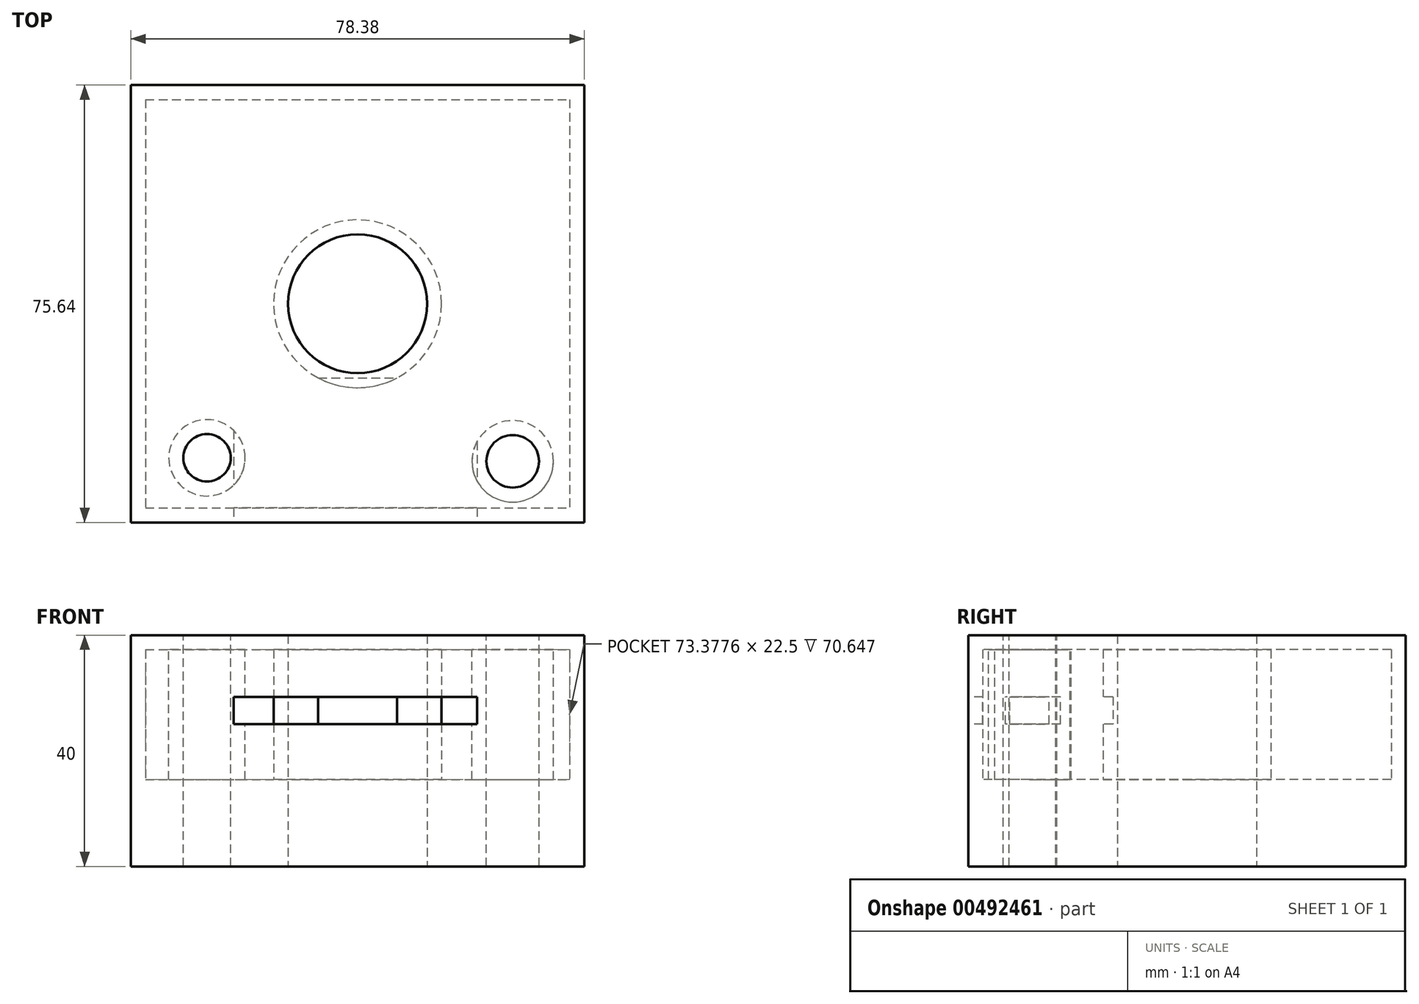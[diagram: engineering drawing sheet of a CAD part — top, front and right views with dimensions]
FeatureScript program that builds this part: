
annotation { "Feature Type Name" : "Feature", "Feature Type Description" : "" }
export const myFeature = defineFeature(function(context is Context, id is Id, definition is map)
    precondition{}
    {
        {
            var Q0;
            Q0=qCreatedBy(makeId("Top.planeOp"),FACE);
            var sketch = newSketch(context, id + "F0", { "sketchPlane" : qUnion([Q0])});
            skLineSegment(sketch, "E0.bottom", {"start": v(-39.19, 37.82) * mm, "end": v(39.19, 37.82) * mm});
            skLineSegment(sketch, "E0.top", {"start": v(-39.19, -37.82) * mm, "end": v(39.19, -37.82) * mm});
            skLineSegment(sketch, "E0.left", {"start": v(-39.19, 37.82) * mm, "end": v(-39.19, -37.82) * mm});
            skLineSegment(sketch, "E0.right", {"start": v(39.19, 37.82) * mm, "end": v(39.19, -37.82) * mm});
            skPoint(sketch, "E0.middle", {"position": v(0, 0) * mm});
            skSolve(sketch);
        }
        {
            var Q0;
            Q0 = qSketchRegion(id + "F0", true);
            extrude(context, id + "F1", {"entities" : qUnion([Q0]), "depth" : 25 * mm});
        }
        {
            var Q0;
            Q0=makeQuery(id+"F1.opExtrude","CAP_FACE",FACE,{"disambiguationData":[OSD([sQuery(id+"F0.wireOp",EDGE,"E0.bottom"),sQuery(id+"F0.wireOp",EDGE,"E0.top"),sQuery(id+"F0.wireOp",EDGE,"E0.left"),sQuery(id+"F0.wireOp",EDGE,"E0.right")])],"isStart":true});
            var sketch = newSketch(context, id + "F2", { "sketchPlane" : qUnion([Q0])});
            skCircle(sketch, "E1", {"center": v(0, 0) * mm, "radius": 12.02 * mm});
            skSolve(sketch);
        }
        {
            var Q0;
            Q0 = qSketchRegion(id + "F2", true);
            extrude(context, id + "F3", {"entities" : qUnion([Q0]), "operationType" : NewBodyOperationType.REMOVE, "oppositeDirection" : true, "depth" : 49.9 * mm});
        }
        {
            var Q0;
            Q0=makeQuery(id+"F1.opExtrude","CAP_FACE",FACE,{"disambiguationData":[OSD([sQuery(id+"F0.wireOp",EDGE,"E0.bottom"),sQuery(id+"F0.wireOp",EDGE,"E0.top"),sQuery(id+"F0.wireOp",EDGE,"E0.left"),sQuery(id+"F0.wireOp",EDGE,"E0.right")])],"isStart":true});
            shell(context, id + "F4", {"entities" : qUnion([Q0]), "thickness" : 2.5 * mm});
        }
        {
            var Q0;
            {var subQ0=sQuery(id+"F0.wireOp",EDGE,"E0.right");var subQ1=sQuery(id+"F0.wireOp",EDGE,"E0.left");var subQ2=sQuery(id+"F0.wireOp",EDGE,"E0.top");var subQ3=sQuery(id+"F0.wireOp",EDGE,"E0.bottom");Q0=makeQuery(id+"F4.opShell","OFFSET_FACE",FACE,{"disambiguationData":[OSD([subQ3,subQ2,subQ1,subQ0]),TDD([makeQuery(id+"F1.opExtrude","CAP_FACE",FACE,{"disambiguationData":[OSD([subQ3,subQ2,subQ1,subQ0])],"isStart":false})])]});}
            var sketch = newSketch(context, id + "F5", { "sketchPlane" : qUnion([Q0])});
            skCircle(sketch, "E2", {"center": v(-26.05, 26.65) * mm, "radius": 6.6 * mm});
            skSolve(sketch);
        }
        {
            var Q0;
            Q0 = qSketchRegion(id + "F5", true);
            extrude(context, id + "F6", {"entities" : qUnion([Q0]), "operationType" : NewBodyOperationType.ADD, "depth" : 25 * mm});
        }
        {
            var Q0;
            Q0=makeQuery(id+"F6.opExtrude","CAP_FACE",FACE,{"disambiguationData":[OSD([sQuery(id+"F5.wireOp",EDGE,"E2")])],"isStart":false});
            shell(context, id + "F7", {"entities" : qUnion([Q0]), "thickness" : 2.5 * mm});
        }
        {
            var Q0;
            Q0=makeQuery(id+"F7.opShell","OFFSET_FACE",FACE,{"disambiguationData":[OSD([sQuery(id+"F0.wireOp",EDGE,"E0.bottom"),sQuery(id+"F0.wireOp",EDGE,"E0.top"),sQuery(id+"F0.wireOp",EDGE,"E0.left"),sQuery(id+"F0.wireOp",EDGE,"E0.right")])]});
            extrude(context, id + "F8", {"entities" : qUnion([Q0]), "operationType" : NewBodyOperationType.REMOVE, "oppositeDirection" : true, "depth" : 25 * mm});
        }
        {
            var Q0;
            {var subQ0=sQuery(id+"F0.wireOp",EDGE,"E0.right");var subQ1=sQuery(id+"F0.wireOp",EDGE,"E0.left");var subQ2=sQuery(id+"F0.wireOp",EDGE,"E0.top");var subQ3=sQuery(id+"F0.wireOp",EDGE,"E0.bottom");Q0=makeQuery(id+"F4.opShell","OFFSET_FACE",FACE,{"disambiguationData":[OSD([subQ3,subQ2,subQ1,subQ0]),TDD([makeQuery(id+"F1.opExtrude","CAP_FACE",FACE,{"disambiguationData":[OSD([subQ3,subQ2,subQ1,subQ0])],"isStart":false})])]});}
            var sketch = newSketch(context, id + "F9", { "sketchPlane" : qUnion([Q0])});
            skCircle(sketch, "E3", {"center": v(26.83, 27.25) * mm, "radius": 7.05 * mm});
            skSolve(sketch);
        }
        {
            var Q0;
            Q0 = qSketchRegion(id + "F9", true);
            extrude(context, id + "F10", {"entities" : qUnion([Q0]), "operationType" : NewBodyOperationType.ADD, "depth" : 25 * mm});
        }
        {
            var Q0;
            Q0=makeQuery(id+"F10.opExtrude","CAP_FACE",FACE,{"disambiguationData":[OSD([sQuery(id+"F9.wireOp",EDGE,"E3")])],"isStart":false});
            shell(context, id + "F11", {"entities" : qUnion([Q0]), "thickness" : 2.5 * mm});
        }
        {
            var Q0;
            Q0=makeQuery(id+"F11.opShell","OFFSET_FACE",FACE,{"disambiguationData":[OSD([sQuery(id+"F0.wireOp",EDGE,"E0.bottom"),sQuery(id+"F0.wireOp",EDGE,"E0.top"),sQuery(id+"F0.wireOp",EDGE,"E0.left"),sQuery(id+"F0.wireOp",EDGE,"E0.right")])]});
            extrude(context, id + "F12", {"entities" : qUnion([Q0]), "operationType" : NewBodyOperationType.REMOVE, "oppositeDirection" : true, "depth" : 25 * mm});
        }
        {
            var Q0;
            Q0=makeQuery(id+"F1.opExtrude","SWEPT_FACE",FACE,{"disambiguationData":[OSD([sQuery(id+"F0.wireOp",EDGE,"E0.top")])]});
            var sketch = newSketch(context, id + "F13", { "sketchPlane" : qUnion([Q0])});
            skLineSegment(sketch, "E4.bottom", {"start": v(-21.45, 14.33) * mm, "end": v(20.66, 14.33) * mm});
            skLineSegment(sketch, "E4.top", {"start": v(-21.45, 9.64) * mm, "end": v(20.66, 9.64) * mm});
            skLineSegment(sketch, "E4.left", {"start": v(-21.45, 14.33) * mm, "end": v(-21.45, 9.64) * mm});
            skLineSegment(sketch, "E4.right", {"start": v(20.66, 14.33) * mm, "end": v(20.66, 9.64) * mm});
            skSolve(sketch);
        }
        {
            var Q0;
            Q0=makeQuery(id+"F13.imprint","IMPRINT",FACE,{"disambiguationData":[TD([[makeQuery(id+"F13.imprint","IMPRINT",EDGE,{"derivedFrom":sQuery(id+"F13.wireOp",EDGE,"E4.bottom")}),-1.0]])]});
            extrude(context, id + "F14", {"entities" : qUnion([Q0]), "operationType" : NewBodyOperationType.REMOVE, "oppositeDirection" : true, "depth" : 25 * mm});
        }
        {
            var Q0;
            Q0=makeQuery(id+"F1.opExtrude","CAP_FACE",FACE,{"disambiguationData":[OSD([sQuery(id+"F0.wireOp",EDGE,"E0.bottom"),sQuery(id+"F0.wireOp",EDGE,"E0.top"),sQuery(id+"F0.wireOp",EDGE,"E0.left"),sQuery(id+"F0.wireOp",EDGE,"E0.right")])],"isStart":true});
            var sketch = newSketch(context, id + "F15", { "sketchPlane" : qUnion([Q0])});
            skLineSegment(sketch, "E5.bottom", {"start": v(-39.19, -37.82) * mm, "end": v(39.19, -37.82) * mm});
            skLineSegment(sketch, "E5.top", {"start": v(-39.19, 37.82) * mm, "end": v(39.19, 37.82) * mm});
            skLineSegment(sketch, "E5.left", {"start": v(-39.19, -37.82) * mm, "end": v(-39.19, 37.82) * mm});
            skLineSegment(sketch, "E5.right", {"start": v(39.19, -37.82) * mm, "end": v(39.19, 37.82) * mm});
            skSolve(sketch);
        }
        {
            var Q0;
            Q0 = qSketchRegion(id + "F15", true);
            extrude(context, id + "F16", {"entities" : qUnion([Q0]), "operationType" : NewBodyOperationType.ADD, "depth" : 15 * mm});
        }
        {
            var Q0;
            Q0=makeQuery(id+"F16.opExtrude","CAP_FACE",FACE,{"disambiguationData":[OSD([sQuery(id+"F15.wireOp",EDGE,"E5.bottom"),sQuery(id+"F15.wireOp",EDGE,"E5.top"),sQuery(id+"F15.wireOp",EDGE,"E5.left"),sQuery(id+"F15.wireOp",EDGE,"E5.right")])],"isStart":false});
            var sketch = newSketch(context, id + "F17", { "sketchPlane" : qUnion([Q0])});
            skCircle(sketch, "E6", {"center": v(-27.18, 22.47) * mm, "radius": 10.6 * mm});
            skSolve(sketch);
        }
        {
            var Q0;
            Q0 = qSketchRegion(id + "F17", true);
            extrude(context, id + "F18", {"entities" : qUnion([Q0]), "operationType" : NewBodyOperationType.REMOVE, "depth" : 25 * mm});
        }
        {
            var Q0;
            Q0=makeQuery(id+"F16.boolean.opBoolean","SPLIT",FACE,{"disambiguationData":[TD([makeQuery(id+"F3.boolean.opBoolean","COPY",FACE,{"derivedFrom":makeQuery(id+"F3.opExtrude","SWEPT_FACE",FACE,{"disambiguationData":[OSD([sQuery(id+"F2.wireOp",EDGE,"E1")])]})})])],"derivedFrom":makeQuery(id+"F16.opExtrude","CAP_FACE",FACE,{"disambiguationData":[OSD([sQuery(id+"F15.wireOp",EDGE,"E5.bottom"),sQuery(id+"F15.wireOp",EDGE,"E5.top"),sQuery(id+"F15.wireOp",EDGE,"E5.left"),sQuery(id+"F15.wireOp",EDGE,"E5.right")])],"isStart":true})});
            extrude(context, id + "F19", {"entities" : qUnion([Q0]), "operationType" : NewBodyOperationType.REMOVE, "oppositeDirection" : true, "depth" : 25 * mm});
        }
        {
            var Q0;
            {var subQ0=sQuery(id+"F5.wireOp",EDGE,"E2");Q0=makeQuery(id+"F16.boolean.opBoolean","SPLIT",FACE,{"disambiguationData":[TD([makeQuery(id+"F7.opShell","OFFSET_FACE",FACE,{"disambiguationData":[OSD([subQ0])]})])],"derivedFrom":makeQuery(id+"F16.opExtrude","CAP_FACE",FACE,{"disambiguationData":[OSD([sQuery(id+"F15.wireOp",EDGE,"E5.bottom"),sQuery(id+"F15.wireOp",EDGE,"E5.top"),sQuery(id+"F15.wireOp",EDGE,"E5.left"),sQuery(id+"F15.wireOp",EDGE,"E5.right")])],"isStart":true})});}
            extrude(context, id + "F20", {"entities" : qUnion([Q0]), "operationType" : NewBodyOperationType.REMOVE, "oppositeDirection" : true, "depth" : 25 * mm});
        }
        {
            var Q0;
            {var subQ0=sQuery(id+"F9.wireOp",EDGE,"E3");Q0=makeQuery(id+"F16.boolean.opBoolean","SPLIT",FACE,{"disambiguationData":[TD([makeQuery(id+"F11.opShell","OFFSET_FACE",FACE,{"disambiguationData":[OSD([subQ0])]})])],"derivedFrom":makeQuery(id+"F16.opExtrude","CAP_FACE",FACE,{"disambiguationData":[OSD([sQuery(id+"F15.wireOp",EDGE,"E5.bottom"),sQuery(id+"F15.wireOp",EDGE,"E5.top"),sQuery(id+"F15.wireOp",EDGE,"E5.left"),sQuery(id+"F15.wireOp",EDGE,"E5.right")])],"isStart":true})});}
            extrude(context, id + "F21", {"entities" : qUnion([Q0]), "operationType" : NewBodyOperationType.REMOVE, "oppositeDirection" : true, "depth" : 25 * mm});
        }
    });
